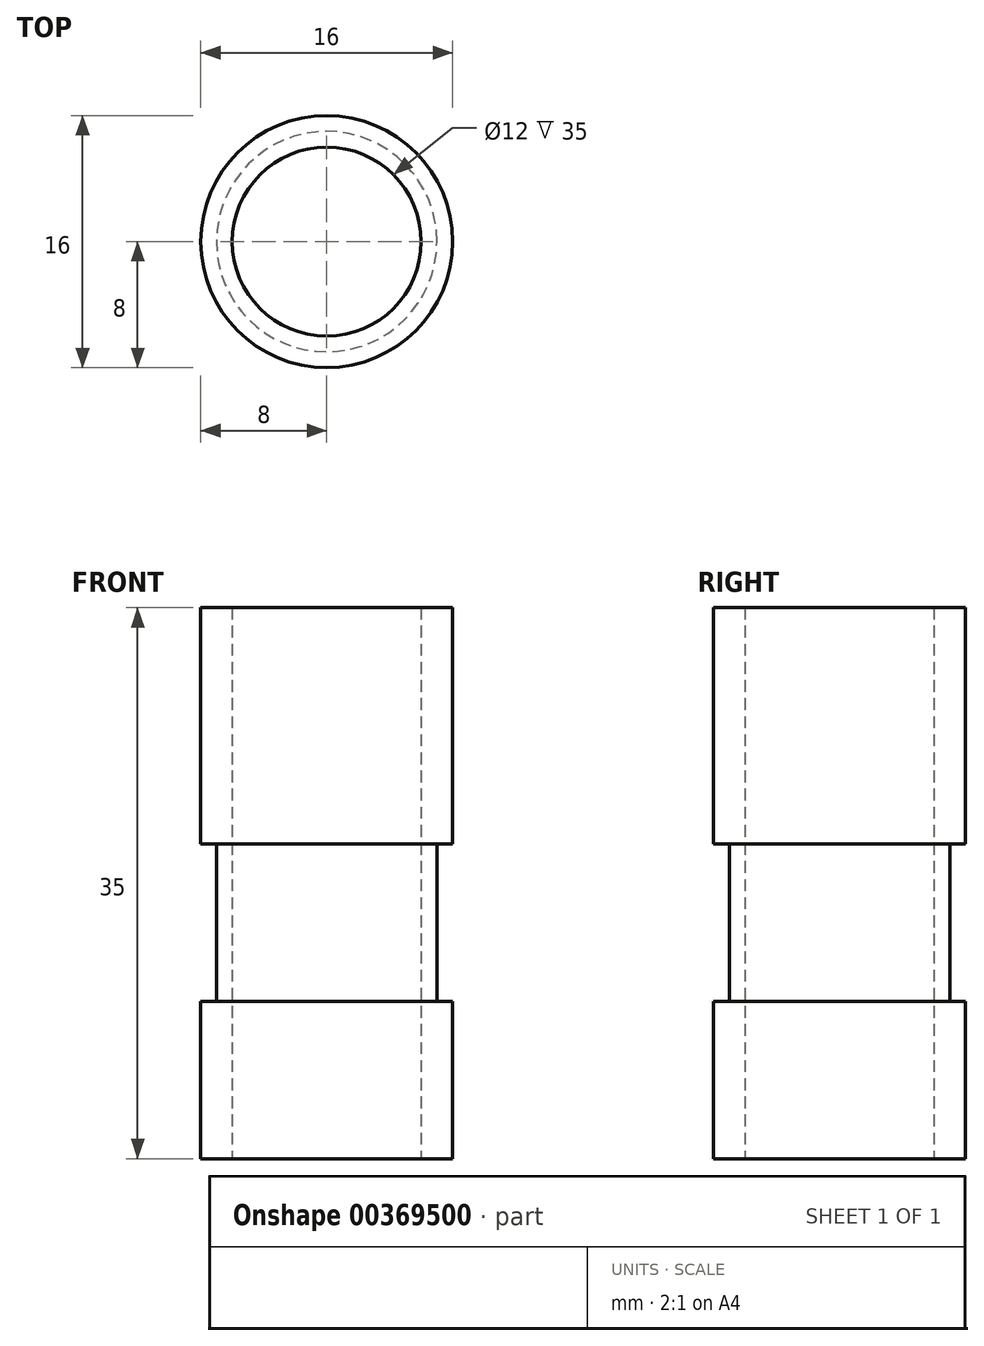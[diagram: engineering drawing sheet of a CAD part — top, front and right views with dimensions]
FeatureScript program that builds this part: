
annotation { "Feature Type Name" : "Feature", "Feature Type Description" : "" }
export const myFeature = defineFeature(function(context is Context, id is Id, definition is map)
    precondition{}
    {
        {
            var Q0;
            Q0=qCreatedBy(makeId("Right.planeOp"),FACE);
            var sketch = newSketch(context, id + "F0", { "sketchPlane" : qUnion([Q0])});
            skLineSegment(sketch, "E0.bottom", {"start": v(0, 0) * mm, "end": v(-6, 0) * mm});
            skLineSegment(sketch, "E0.top", {"start": v(0, 35) * mm, "end": v(-6, 35) * mm});
            skLineSegment(sketch, "E0.left", {"start": v(0, 0) * mm, "end": v(0, 35) * mm});
            skLineSegment(sketch, "E0.right", {"start": v(-6, 0) * mm, "end": v(-6, 35) * mm});
            skLineSegment(sketch, "E1.bottom", {"start": v(-6, 35) * mm, "end": v(-8, 35) * mm});
            skLineSegment(sketch, "E1.top", {"start": v(-6, 0) * mm, "end": v(-8, 0) * mm});
            skLineSegment(sketch, "E1.left", {"start": v(-6, 35) * mm, "end": v(-6, 0) * mm});
            skLineSegment(sketch, "E1.right", {"start": v(-8, 35) * mm, "end": v(-8, 0) * mm});
            skLineSegment(sketch, "E2.bottom", {"start": v(-8, 20) * mm, "end": v(-7, 20) * mm});
            skLineSegment(sketch, "E2.top", {"start": v(-8, 10) * mm, "end": v(-7, 10) * mm});
            skLineSegment(sketch, "E2.left", {"start": v(-8, 20) * mm, "end": v(-8, 10) * mm});
            skLineSegment(sketch, "E2.right", {"start": v(-7, 20) * mm, "end": v(-7, 10) * mm});
            skSolve(sketch);
        }
        {
            var Q0;
            {var subQ1=sQuery(id+"F0.wireOp",EDGE,"E1.bottom");Q0=makeQuery(id+"F0.imprint","IMPRINT",FACE,{"disambiguationData":[TD([[makeQuery(id+"F0.imprint","IMPRINT",EDGE,{"derivedFrom":subQ1}),1.0]])]});}
            var Q1;
            Q1=sQuery(id+"F0.wireOp",EDGE,"E0.left");
            revolve(context, id + "F1", {"entities" : qUnion([Q0]), "axis" : qUnion([Q1]), "revolveType" : RevolveType.FULL});
        }
    });
